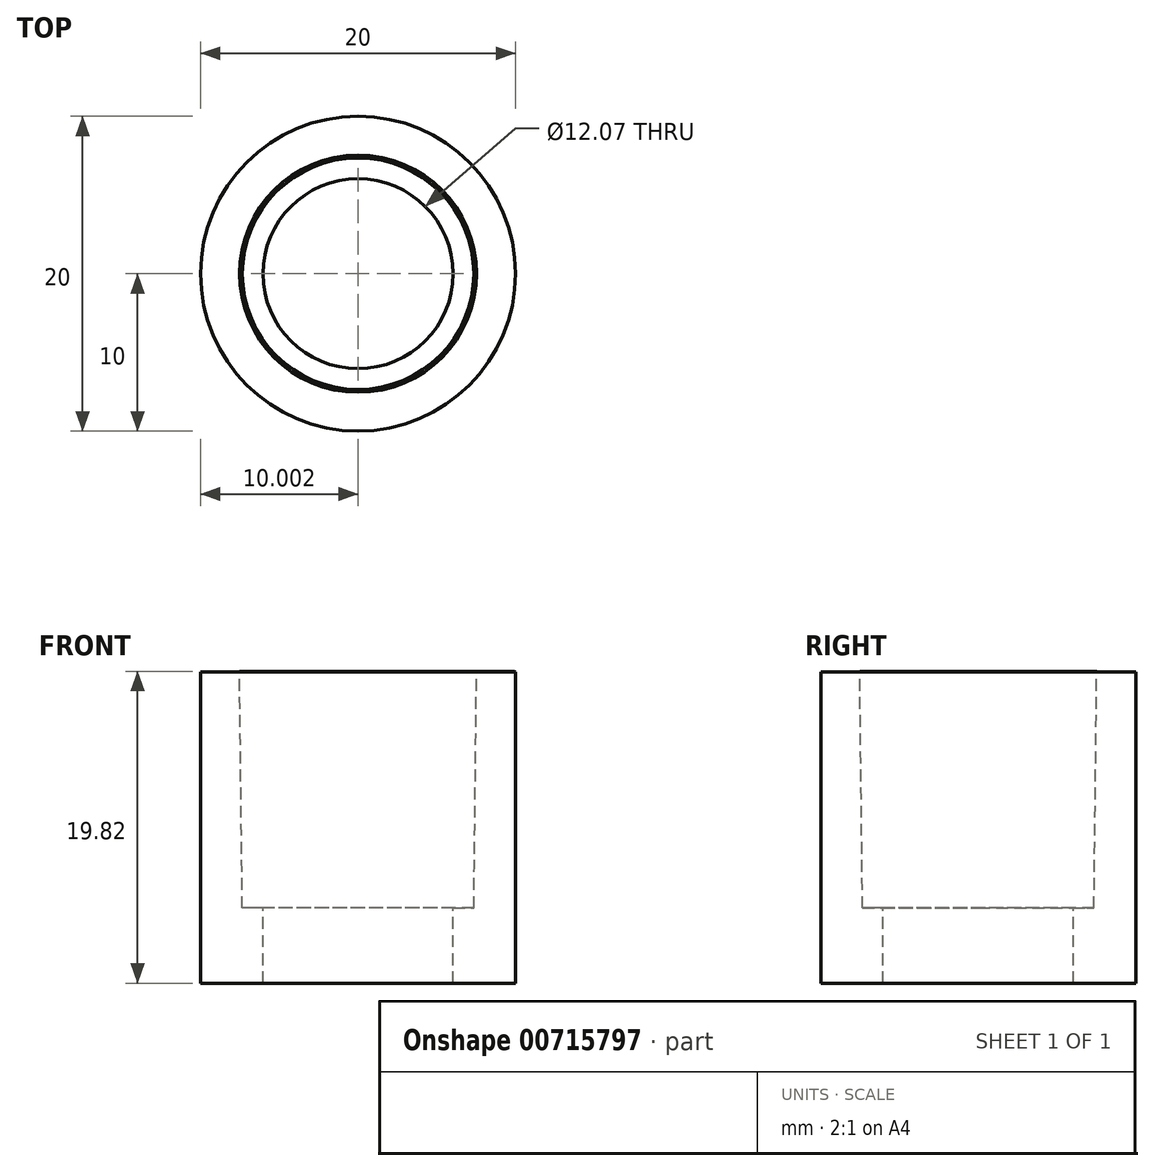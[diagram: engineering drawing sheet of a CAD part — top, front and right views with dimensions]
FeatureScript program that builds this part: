
annotation { "Feature Type Name" : "Feature", "Feature Type Description" : "" }
export const myFeature = defineFeature(function(context is Context, id is Id, definition is map)
    precondition{}
    {
        {
            var Q0;
            Q0=qCreatedBy(makeId("Front.planeOp"),FACE);
            var sketch = newSketch(context, id + "F0", { "sketchPlane" : qUnion([Q0])});
            skPoint(sketch, "E0.middle", {"position": v(-32.46, 12.42) * mm});
            skLineSegment(sketch, "E1.bottom", {"start": v(-22.46, 0.5) * mm, "end": v(-26.42, 0.5) * mm});
            skLineSegment(sketch, "E1.left", {"start": v(-22.46, 0.5) * mm, "end": v(-22.46, 20.28) * mm});
            skPoint(sketch, "E2.orphan", {"position": v(-22.46, 24.36) * mm});
            skLineSegment(sketch, "E3", {"start": v(-25.1, 5.27) * mm, "end": v(-24.93, 20.3) * mm});
            skPoint(sketch, "E0.left.start.orphan", {"position": v(-25.6, 20.17) * mm});
            skLineSegment(sketch, "E4", {"start": v(-22.46, 20.28) * mm, "end": v(-24.93, 20.3) * mm});
            skLineSegment(sketch, "E5", {"start": v(-32.46, 20.4) * mm, "end": v(-32.46, 0.5) * mm});
            skLineSegment(sketch, "E6", {"start": v(-25.1, 5.27) * mm, "end": v(-26.42, 5.28) * mm});
            skLineSegment(sketch, "E7", {"start": v(-26.42, 5.28) * mm, "end": v(-26.42, 0.5) * mm});
            skSolve(sketch);
        }
        {
            var Q0;
            Q0=makeQuery(id+"F0.imprint","IMPRINT",FACE,{"disambiguationData":[TD([[makeQuery(id+"F0.imprint","IMPRINT",EDGE,{"derivedFrom":sQuery(id+"F0.wireOp",EDGE,"E1.bottom")}),-1.0]])]});
            var Q1;
            Q1=sQuery(id+"F0.wireOp",EDGE,"E5");
            revolve(context, id + "F1", {"surfaceOperationType" : NewSurfaceOperationType.NEW, "entities" : qUnion([Q0]), "axis" : qUnion([Q1]), "revolveType" : RevolveType.FULL});
        }
    });
